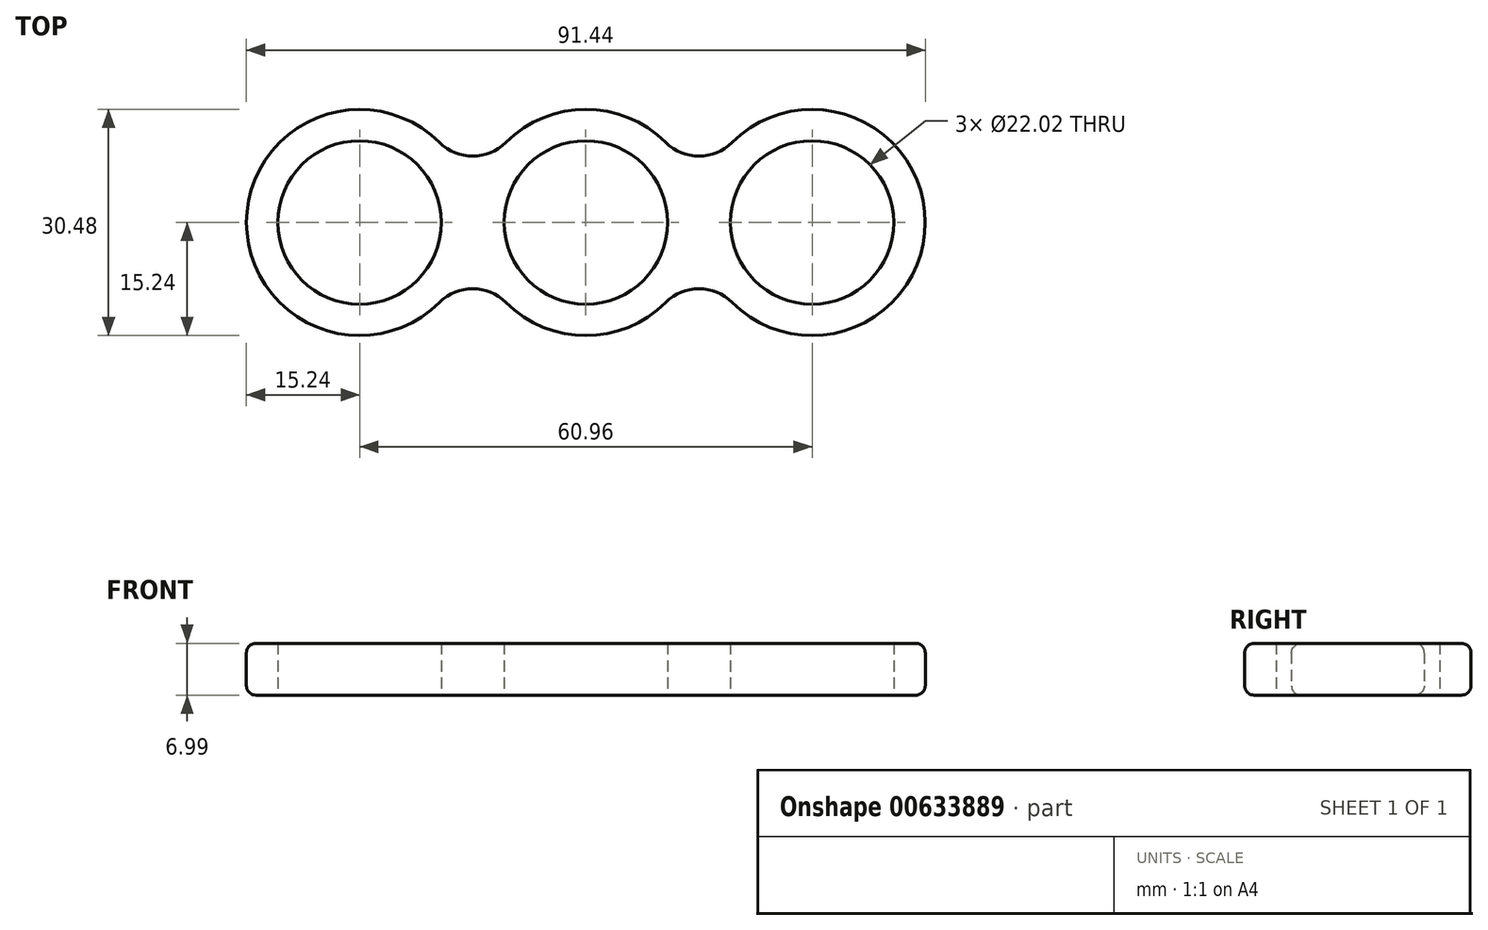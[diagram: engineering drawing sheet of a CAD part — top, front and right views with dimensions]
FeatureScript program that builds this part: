
annotation { "Feature Type Name" : "Feature", "Feature Type Description" : "" }
export const myFeature = defineFeature(function(context is Context, id is Id, definition is map)
    precondition{}
    {
        {
            var Q0;
            Q0=qCreatedBy(makeId("Top.planeOp"),FACE);
            var sketch = newSketch(context, id + "F0", { "sketchPlane" : qUnion([Q0])});
            skCircle(sketch, "E0", {"center": v(0, 0) * mm, "radius": 11.01 * mm});
            skCircle(sketch, "E1", {"center": v(30.48, 0) * mm, "radius": 11.01 * mm});
            skCircle(sketch, "E2", {"center": v(-30.48, 0) * mm, "radius": 11.01 * mm});
            skLineSegment(sketch, "E3", {"start": v(-30.48, 0) * mm, "end": v(0, 0) * mm});
            skLineSegment(sketch, "E4", {"start": v(0, 0) * mm, "end": v(30.48, 0) * mm});
            skCircle(sketch, "E5", {"center": v(-30.48, 0) * mm, "radius": 15.24 * mm});
            skCircle(sketch, "E6", {"center": v(0, 0) * mm, "radius": 15.24 * mm});
            skCircle(sketch, "E7", {"center": v(30.48, 0) * mm, "radius": 15.24 * mm});
            skArc(sketch, "E8", {"start": v(-19.72, 10.8) * mm, "mid": v(-15.24, 8.94) * mm, "end": v(-10.76, 10.8) * mm});
            skArc(sketch, "E9", {"start": v(10.76, 10.8) * mm, "mid": v(15.24, 8.94) * mm, "end": v(19.72, 10.8) * mm});
            skArc(sketch, "E10", {"start": v(-10.76, -10.8) * mm, "mid": v(-15.24, -8.94) * mm, "end": v(-19.72, -10.8) * mm});
            skArc(sketch, "E11", {"start": v(19.72, -10.8) * mm, "mid": v(15.24, -8.94) * mm, "end": v(10.76, -10.8) * mm});
            skSolve(sketch);
        }
        {
            var Q0;
            Q0 = qSketchRegion(id + "F0", true);
            extrude(context, id + "F1", {"entities" : qUnion([Q0]), "depth" : 7 * mm, "offsetDistance" : 25.4 * mm});
        }
        {
            var Q0;
            Q0=makeQuery(id+"F1.opExtrude","CAP_EDGE",EDGE,{"disambiguationData":[OSD([sQuery(id+"F0.wireOp",EDGE,"E5")])],"isStart":false});
            var Q1;
            {var subQ0=sQuery(id+"F0.wireOp",EDGE,"E6");Q1=makeQuery(id+"F1.opExtrude","CAP_EDGE",EDGE,{"disambiguationData":[OSD([subQ0]),TDD([makeQuery(id+"F0.imprint","IMPRINT",EDGE,{"disambiguationData":[TD([[makeQuery(id+"F0.imprint","INTERSECT",VERTEX,{"derivedFrom":[subQ0,sQuery(id+"F0.wireOp",EDGE,"E8")]}),1.0]])],"derivedFrom":subQ0})])],"isStart":false});}
            var Q2;
            {var subQ0=sQuery(id+"F0.wireOp",EDGE,"E6");Q2=makeQuery(id+"F1.opExtrude","CAP_EDGE",EDGE,{"disambiguationData":[OSD([subQ0]),TDD([makeQuery(id+"F0.imprint","IMPRINT",EDGE,{"disambiguationData":[TD([[makeQuery(id+"F0.imprint","INTERSECT",VERTEX,{"derivedFrom":[subQ0,sQuery(id+"F0.wireOp",EDGE,"E10")]}),-1.0]])],"derivedFrom":subQ0})])],"isStart":false});}
            var Q3;
            Q3=makeQuery(id+"F1.opExtrude","CAP_EDGE",EDGE,{"disambiguationData":[OSD([sQuery(id+"F0.wireOp",EDGE,"E10")])],"isStart":false});
            var Q4;
            Q4=makeQuery(id+"F1.opExtrude","CAP_EDGE",EDGE,{"disambiguationData":[OSD([sQuery(id+"F0.wireOp",EDGE,"E8")])],"isStart":false});
            var Q5;
            Q5=makeQuery(id+"F1.opExtrude","CAP_EDGE",EDGE,{"disambiguationData":[OSD([sQuery(id+"F0.wireOp",EDGE,"E9")])],"isStart":false});
            var Q6;
            Q6=makeQuery(id+"F1.opExtrude","CAP_EDGE",EDGE,{"disambiguationData":[OSD([sQuery(id+"F0.wireOp",EDGE,"E7")])],"isStart":false});
            var Q7;
            Q7=makeQuery(id+"F1.opExtrude","CAP_EDGE",EDGE,{"disambiguationData":[OSD([sQuery(id+"F0.wireOp",EDGE,"E11")])],"isStart":false});
            var Q8;
            Q8=makeQuery(id+"F1.opExtrude","CAP_EDGE",EDGE,{"disambiguationData":[OSD([sQuery(id+"F0.wireOp",EDGE,"E5")])],"isStart":true});
            var Q9;
            {var subQ0=sQuery(id+"F0.wireOp",EDGE,"E6");Q9=makeQuery(id+"F1.opExtrude","CAP_EDGE",EDGE,{"disambiguationData":[OSD([subQ0]),TDD([makeQuery(id+"F0.imprint","IMPRINT",EDGE,{"disambiguationData":[TD([[makeQuery(id+"F0.imprint","INTERSECT",VERTEX,{"derivedFrom":[subQ0,sQuery(id+"F0.wireOp",EDGE,"E10")]}),-1.0]])],"derivedFrom":subQ0})])],"isStart":true});}
            var Q10;
            Q10=makeQuery(id+"F1.opExtrude","CAP_EDGE",EDGE,{"disambiguationData":[OSD([sQuery(id+"F0.wireOp",EDGE,"E7")])],"isStart":true});
            var Q11;
            Q11=makeQuery(id+"F1.opExtrude","CAP_EDGE",EDGE,{"disambiguationData":[OSD([sQuery(id+"F0.wireOp",EDGE,"E9")])],"isStart":true});
            var Q12;
            {var subQ0=sQuery(id+"F0.wireOp",EDGE,"E6");Q12=makeQuery(id+"F1.opExtrude","CAP_EDGE",EDGE,{"disambiguationData":[OSD([subQ0]),TDD([makeQuery(id+"F0.imprint","IMPRINT",EDGE,{"disambiguationData":[TD([[makeQuery(id+"F0.imprint","INTERSECT",VERTEX,{"derivedFrom":[subQ0,sQuery(id+"F0.wireOp",EDGE,"E8")]}),1.0]])],"derivedFrom":subQ0})])],"isStart":true});}
            var Q13;
            Q13=makeQuery(id+"F1.opExtrude","CAP_EDGE",EDGE,{"disambiguationData":[OSD([sQuery(id+"F0.wireOp",EDGE,"E8")])],"isStart":true});
            var Q14;
            Q14=makeQuery(id+"F1.opExtrude","CAP_EDGE",EDGE,{"disambiguationData":[OSD([sQuery(id+"F0.wireOp",EDGE,"E11")])],"isStart":true});
            var Q15;
            Q15=makeQuery(id+"F1.opExtrude","CAP_EDGE",EDGE,{"disambiguationData":[OSD([sQuery(id+"F0.wireOp",EDGE,"E10")])],"isStart":true});
            fillet(context, id + "F2", {"entities" : qUnion([Q0, Q1, Q2, Q3, Q4, Q5, Q6, Q7, Q8, Q9, Q10, Q11, Q12, Q13, Q14, Q15]), "radius" : 1.27 * mm, "tangentPropagation" : true, "allowEdgeOverflow" : false});
        }
    });
